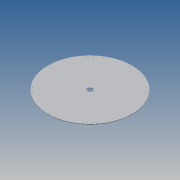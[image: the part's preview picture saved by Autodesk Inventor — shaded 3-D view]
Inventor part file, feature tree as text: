
AUTODESK INVENTOR PART (.ipt)
format: ipt  version: 2014 SP1 (Build 180222100, 222)  size: 186,368 bytes
history: native  units: in
note: dims shown in document units (in); Inventor stores cm internally (conversion verified against a paired STEP export)
features: sketch x5, hole x3, pattern_circular x3, extrude x2
ambient origin geometry x8: Origin, YZ Plane, XZ Plane, XY Plane, X Axis, Y Axis, Z Axis, Center Point
bodies: Body1 (feature_tree)
feature tree (13):
  extrude  "Extrusion1"  Depth=0.125in TaperAngle=0.0deg
  extrude  "Extrusion2"  Depth=0.125in TaperAngle=0.0deg
  hole  "Hole1"  [1 undecoded]
  pattern_circular  "Circular Pattern1"  Angle=45.0deg  [1 undecoded]
  hole  "Hole2"  [1 undecoded]
  pattern_circular  "Circular Pattern2"  [2 undecoded]
  hole  "Hole3"  [1 undecoded]
  pattern_circular  "Circular Pattern3"  [2 undecoded]
  sketch  "Sketch1"  dims[d0=24.0in d1=0.125in d2=0.0in]
  sketch  "Sketch2"  dims[d3=1.5in d4=0.125in d5=0.0in]
  sketch  "Sketch3"  dims[d6=11.5in]
  sketch  "Sketch4"  dims[d7=0.177in d8=0.2362in d9=0.332in d10=0.0787in d11=0.5635in d12=0.315in d13=0.8108in d14=1.5748in d15=360.0deg]
  sketch  "Sketch5"  dims[d20=11.5in d21=45.0deg d22=0.719in d23=0.719in d24=0.177in d25=0.2362in d26=0.332in d27=0.0787in d28=0.5635in d29=0.315in d30=0.8108in d31=1.5748in d32=360.0deg d34=0.875in d35=0.096in d36=0.2362in d37=0.172in d38=0.0787in d39=0.5635in d40=0.315in d41=0.8108in d42=1.5748in d43=360.0deg]
note: 8 required parameter values undecoded (feature->parameter linkage not recoverable at this tier; creation-order binding heuristic only, values carry confidence <= 0.55)
